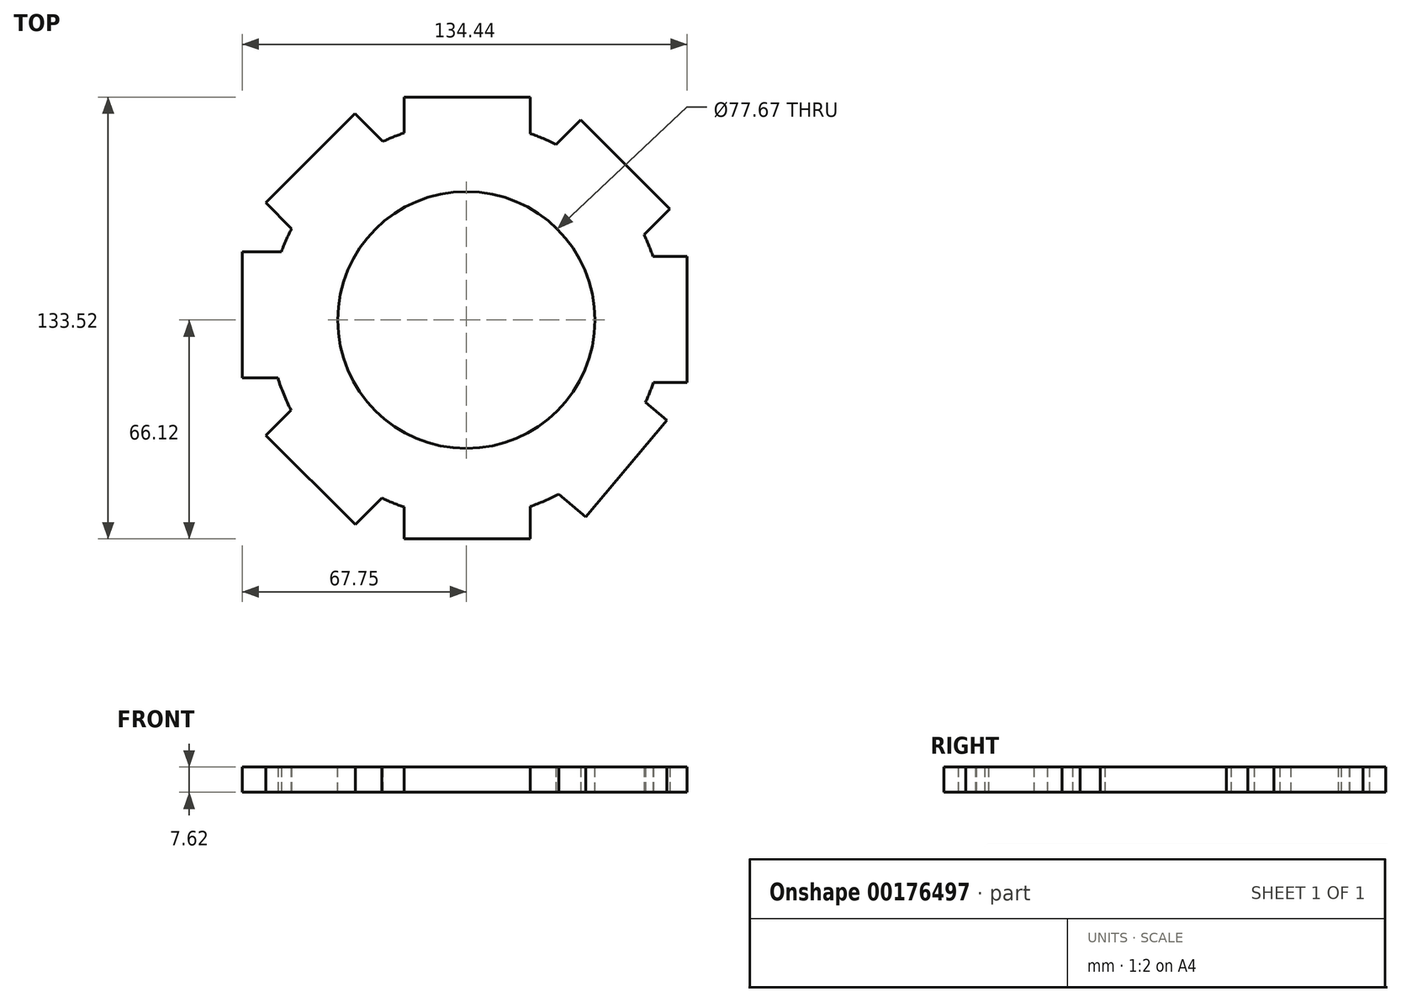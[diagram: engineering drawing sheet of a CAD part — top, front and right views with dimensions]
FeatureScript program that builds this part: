
annotation { "Feature Type Name" : "Feature", "Feature Type Description" : "" }
export const myFeature = defineFeature(function(context is Context, id is Id, definition is map)
    precondition{}
    {
        {
            var Q0;
            Q0=qCreatedBy(makeId("Top.planeOp"),FACE);
            var sketch = newSketch(context, id + "F0", { "sketchPlane" : qUnion([Q0])});
            skCircle(sketch, "E0", {"center": v(0, 0) * mm, "radius": 59.57 * mm});
            skSolve(sketch);
        }
        {
            var Q0;
            Q0 = qSketchRegion(id + "F0", true);
            extrude(context, id + "F1", {"entities" : qUnion([Q0]), "endBound" : BoundingType.SYMMETRIC, "depth" : 7.62 * mm});
        }
        {
            var Q0;
            Q0=makeQuery(id+"F1.opExtrude","CAP_FACE",FACE,{"disambiguationData":[OSD([sQuery(id+"F0.wireOp",EDGE,"E0")])],"isStart":false});
            var sketch = newSketch(context, id + "F2", { "sketchPlane" : qUnion([Q0])});
            skCircle(sketch, "E1", {"center": v(0, 0) * mm, "radius": 38.83 * mm});
            skSolve(sketch);
        }
        {
            var Q0;
            Q0=makeQuery(id+"F2.imprint","IMPRINT",FACE,{"disambiguationData":[TD([[makeQuery(id+"F2.imprint","IMPRINT",EDGE,{"derivedFrom":sQuery(id+"F2.wireOp",EDGE,"E1")}),1.0]])]});
            extrude(context, id + "F3", {"entities" : qUnion([Q0]), "operationType" : NewBodyOperationType.REMOVE, "oppositeDirection" : true, "depth" : 25.4 * mm});
        }
        {
            var Q0;
            Q0=qCreatedBy(makeId("Top.planeOp"),FACE);
            var sketch = newSketch(context, id + "F4", { "sketchPlane" : qUnion([Q0])});
            skLineSegment(sketch, "E2.bottom", {"start": v(-18.82, -66.12) * mm, "end": v(19.28, -66.12) * mm});
            skLineSegment(sketch, "E2.top", {"start": v(-18.82, -53.42) * mm, "end": v(19.28, -53.42) * mm});
            skLineSegment(sketch, "E2.left", {"start": v(-18.82, -66.12) * mm, "end": v(-18.82, -53.42) * mm});
            skLineSegment(sketch, "E2.right", {"start": v(19.28, -66.12) * mm, "end": v(19.28, -53.42) * mm});
            skLineSegment(sketch, "E3.bottom", {"start": v(-18.82, 54.7) * mm, "end": v(19.28, 54.7) * mm});
            skLineSegment(sketch, "E3.top", {"start": v(-18.82, 67.4) * mm, "end": v(19.28, 67.4) * mm});
            skLineSegment(sketch, "E3.left", {"start": v(-18.82, 54.7) * mm, "end": v(-18.82, 67.4) * mm});
            skLineSegment(sketch, "E3.right", {"start": v(19.28, 54.7) * mm, "end": v(19.28, 67.4) * mm});
            skLineSegment(sketch, "E4.bottom", {"start": v(53.99, -18.88) * mm, "end": v(66.69, -18.88) * mm});
            skLineSegment(sketch, "E4.top", {"start": v(53.99, 19.22) * mm, "end": v(66.69, 19.22) * mm});
            skLineSegment(sketch, "E4.left", {"start": v(53.99, -18.88) * mm, "end": v(53.99, 19.22) * mm});
            skLineSegment(sketch, "E4.right", {"start": v(66.69, -18.88) * mm, "end": v(66.69, 19.22) * mm});
            skLineSegment(sketch, "E5.bottom", {"start": v(-67.75, -17.46) * mm, "end": v(-55.05, -17.46) * mm});
            skLineSegment(sketch, "E5.top", {"start": v(-67.75, 20.64) * mm, "end": v(-55.05, 20.64) * mm});
            skLineSegment(sketch, "E5.left", {"start": v(-67.75, -17.46) * mm, "end": v(-67.75, 20.64) * mm});
            skLineSegment(sketch, "E5.right", {"start": v(-55.05, -17.46) * mm, "end": v(-55.05, 20.64) * mm});
            skLineSegment(sketch, "E6.bottom", {"start": v(36.12, -59.55) * mm, "end": v(60.6, -30.36) * mm});
            skLineSegment(sketch, "E6.top", {"start": v(26.39, -51.38) * mm, "end": v(50.88, -22.2) * mm});
            skLineSegment(sketch, "E6.left", {"start": v(36.12, -59.55) * mm, "end": v(26.39, -51.38) * mm});
            skLineSegment(sketch, "E6.right", {"start": v(60.6, -30.36) * mm, "end": v(50.88, -22.2) * mm});
            skLineSegment(sketch, "E7.bottom", {"start": v(-60.53, -34.88) * mm, "end": v(-33.59, -61.82) * mm});
            skLineSegment(sketch, "E7.top", {"start": v(-51.55, -25.9) * mm, "end": v(-24.6, -52.84) * mm});
            skLineSegment(sketch, "E7.left", {"start": v(-60.53, -34.88) * mm, "end": v(-51.55, -25.9) * mm});
            skLineSegment(sketch, "E7.right", {"start": v(-33.59, -61.82) * mm, "end": v(-24.6, -52.84) * mm});
            skLineSegment(sketch, "E8.bottom", {"start": v(25.54, 51.5) * mm, "end": v(52.48, 24.56) * mm});
            skLineSegment(sketch, "E8.top", {"start": v(34.52, 60.48) * mm, "end": v(61.46, 33.54) * mm});
            skLineSegment(sketch, "E8.left", {"start": v(25.54, 51.5) * mm, "end": v(34.52, 60.48) * mm});
            skLineSegment(sketch, "E8.right", {"start": v(52.48, 24.56) * mm, "end": v(61.46, 33.54) * mm});
            skLineSegment(sketch, "E9.bottom", {"start": v(-51.6, 26.46) * mm, "end": v(-24.65, 53.4) * mm});
            skLineSegment(sketch, "E9.top", {"start": v(-60.58, 35.44) * mm, "end": v(-33.63, 62.38) * mm});
            skLineSegment(sketch, "E9.left", {"start": v(-51.6, 26.46) * mm, "end": v(-60.58, 35.44) * mm});
            skLineSegment(sketch, "E9.right", {"start": v(-24.65, 53.4) * mm, "end": v(-33.63, 62.38) * mm});
            skSolve(sketch);
        }
        {
            var Q0;
            Q0=makeQuery(id+"F4.imprint","IMPRINT",FACE,{"disambiguationData":[TD([[makeQuery(id+"F4.imprint","IMPRINT",EDGE,{"derivedFrom":sQuery(id+"F4.wireOp",EDGE,"E7.bottom")}),1.0]])]});
            var Q1;
            Q1=makeQuery(id+"F4.imprint","IMPRINT",FACE,{"disambiguationData":[TD([[makeQuery(id+"F4.imprint","IMPRINT",EDGE,{"derivedFrom":sQuery(id+"F4.wireOp",EDGE,"E6.bottom")}),1.0]])]});
            var Q2;
            Q2=makeQuery(id+"F4.imprint","IMPRINT",FACE,{"disambiguationData":[TD([[makeQuery(id+"F4.imprint","IMPRINT",EDGE,{"derivedFrom":sQuery(id+"F4.wireOp",EDGE,"E4.bottom")}),1.0]])]});
            var Q3;
            Q3=makeQuery(id+"F4.imprint","IMPRINT",FACE,{"disambiguationData":[TD([[makeQuery(id+"F4.imprint","IMPRINT",EDGE,{"derivedFrom":sQuery(id+"F4.wireOp",EDGE,"E2.bottom")}),1.0]])]});
            var Q4;
            Q4=makeQuery(id+"F4.imprint","IMPRINT",FACE,{"disambiguationData":[TD([[makeQuery(id+"F4.imprint","IMPRINT",EDGE,{"derivedFrom":sQuery(id+"F4.wireOp",EDGE,"E5.bottom")}),1.0]])]});
            var Q5;
            Q5=makeQuery(id+"F4.imprint","IMPRINT",FACE,{"disambiguationData":[TD([[makeQuery(id+"F4.imprint","IMPRINT",EDGE,{"derivedFrom":sQuery(id+"F4.wireOp",EDGE,"E9.bottom")}),1.0]])]});
            var Q6;
            Q6=makeQuery(id+"F4.imprint","IMPRINT",FACE,{"disambiguationData":[TD([[makeQuery(id+"F4.imprint","IMPRINT",EDGE,{"derivedFrom":sQuery(id+"F4.wireOp",EDGE,"E3.bottom")}),1.0]])]});
            var Q7;
            Q7=makeQuery(id+"F4.imprint","IMPRINT",FACE,{"disambiguationData":[TD([[makeQuery(id+"F4.imprint","IMPRINT",EDGE,{"derivedFrom":sQuery(id+"F4.wireOp",EDGE,"E8.bottom")}),1.0]])]});
            extrude(context, id + "F5", {"entities" : qUnion([Q0, Q1, Q2, Q3, Q4, Q5, Q6, Q7]), "operationType" : NewBodyOperationType.ADD, "endBound" : BoundingType.SYMMETRIC, "depth" : 7.62 * mm});
        }
    });
